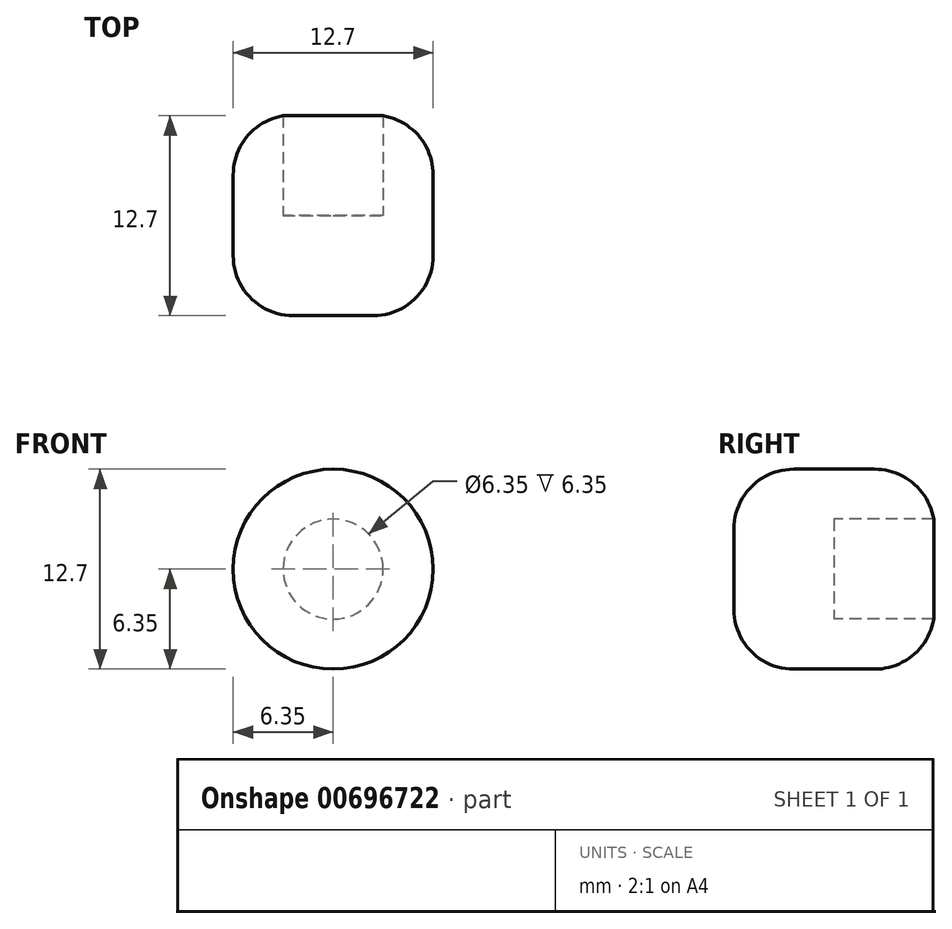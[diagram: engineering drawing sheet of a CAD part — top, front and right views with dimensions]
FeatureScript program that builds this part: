
annotation { "Feature Type Name" : "Feature", "Feature Type Description" : "" }
export const myFeature = defineFeature(function(context is Context, id is Id, definition is map)
    precondition{}
    {
        {
            var Q0;
            Q0=qCreatedBy(makeId("Front.planeOp"),FACE);
            var sketch = newSketch(context, id + "F0", { "sketchPlane" : qUnion([Q0])});
            skCircle(sketch, "E0", {"center": v(0, 0) * mm, "radius": 6.35 * mm});
            skSolve(sketch);
        }
        {
            var Q0;
            Q0 = qSketchRegion(id + "F0", true);
            extrude(context, id + "F1", {"entities" : qUnion([Q0]), "depth" : 6.35 * mm, "offsetDistance" : 25.4 * mm});
        }
        {
            var Q0;
            Q0=makeQuery(id+"F1.opExtrude","CAP_FACE",FACE,{"disambiguationData":[OSD([sQuery(id+"F0.wireOp",EDGE,"E0")])],"isStart":true});
            var sketch = newSketch(context, id + "F2", { "sketchPlane" : qUnion([Q0])});
            skCircle(sketch, "E1", {"center": v(0, 0) * mm, "radius": 3.18 * mm});
            skSolve(sketch);
        }
        {
            var Q0;
            Q0=makeQuery(id+"F2.imprint","IMPRINT",FACE,{"disambiguationData":[TD([[makeQuery(id+"F2.imprint","IMPRINT",EDGE,{"derivedFrom":sQuery(id+"F2.wireOp",EDGE,"E1")}),-1.0]])]});
            extrude(context, id + "F3", {"entities" : qUnion([Q0]), "operationType" : NewBodyOperationType.ADD, "depth" : 6.35 * mm, "offsetDistance" : 25.4 * mm});
        }
        {
            var Q0;
            Q0=makeQuery(id+"F3.opExtrude","CAP_EDGE",EDGE,{"disambiguationData":[OSD([sQuery(id+"F0.wireOp",EDGE,"E0")])],"isStart":false});
            var Q1;
            Q1=makeQuery(id+"F1.opExtrude","CAP_EDGE",EDGE,{"disambiguationData":[OSD([sQuery(id+"F0.wireOp",EDGE,"E0")])],"isStart":false});
            fillet(context, id + "F4", {"entities" : qUnion([Q0, Q1]), "radius" : 3.8 * mm, "tangentPropagation" : true, "allowEdgeOverflow" : false});
        }
    });
